# Revit family: Haworth_BeHold_PersonalStorageTower_HingedBookcase_24Wide
name_source: partatom
category: Furniture Systems
revit_build: Autodesk Revit 2018 (Build: 20170223_1515(x64)
units: mm (PartAtom-declared; Revit-internal decimal feet)

## family parameters
Always vertical = Yes
Cut with Voids When Loaded = No
OmniClass Number = 23.40.70.14.64.21
OmniClass Title = Systems Furniture
Part Type = Normal
Room Calculation Point = No
Round Connector Dimension = Use Diameter
Shared = No
Work Plane-Based = No

## types (8) — shared parameters
Actual Width = 24"
Assembly Code = E2020200
Blade Pull = No
Blade Pull Length = 15 29/64"
Bookcase Width = 15 41/64"
Bottom Case Offset = 1/2"
Bottom Drawer Offset = 1 3/8"
Case Thickness = 3/4"
Classic Pull = No
Classic Pull Length = 7 1/2"
Cresent Pull = No
Custom Size = No
Description = Haworth - Be_Hold - Personal Storage Tower - Hinged Door
Drawer Width = 15 33/64"
Glide Finish = Haworth _ Polymer _ Slate
Linear Pull = No
Linear Pull Length = 7 1/2"
Manufacturer = Haworth
Max. Depth = 24"
Max. Height = 65"
Max. Width = 15"
Min. Depth = 18"
Min. Height = 41"
Min. Width = 15"
Model = Haworth Be_Hold
Revision Number = 1
Shelf 1 Offset = 26 3/4"
Size = Verify Final Dim. w/ Haworth
Standard Depths = 18, 24 in.
Standard Heights = 41, 49, 57, 65 in.
Storage Height = 28"
Sustainability Info = https://www.haworth.com
Top Thickness = 3/4"
Total Drawer Height = 26 1/2"
URL = www.haworth.com
URL - Product = https://www.haworth.com
Valet Door Width = 8 15/64"
Warranty = http://www.haworth.com
Wing Drawer Pull Length = 8 5/16"
Wing Pull = Yes
With Lock = Yes

## per-type parameters (varying)
- B/B/F - 24d 65h - Inset Back: 3 Drawer Control=Yes; Actual Depth=24"; Actual Height=65"; Back Case Back Control=3/16"; Back Case Side Control=3/4"; Bookcase Door Height=36 1/8"; Bookcase Door Pull Offset=18 1/16"; Bottom Drawer Height=13 1/8"; Box Box File=Yes; Depth=24"; Distance Between Drawer=1/4"; File File=No; Height=65"; Inset Style=Yes; Middle Drawer Height=6 9/16"; Proud Style=No; Shelf 2 Control=Yes; Shelf 2 Offset=49"; Side Case Back Control=0"; Top Case Back Control=3/16"; Top Drawer Height=6 9/16"; Valet Door Height=62 3/4"; Valet Door Pull Offset=44 11/16"; Valet Door Wing Pull Length=16 3/4"; Wing Door Pull Length=16 3/4"
- B/B/F - 24d 57h - Inset Back: 3 Drawer Control=Yes; Actual Depth=24"; Actual Height=57"; Back Case Back Control=3/16"; Back Case Side Control=3/4"; Bookcase Door Height=28 1/8"; Bookcase Door Pull Offset=14 1/16"; Bottom Drawer Height=13 1/8"; Box Box File=Yes; Depth=24"; Distance Between Drawer=1/4"; File File=No; Height=57"; Inset Style=Yes; Middle Drawer Height=6 9/16"; Proud Style=No; Shelf 2 Control=Yes; Shelf 2 Offset=41"; Side Case Back Control=0"; Top Case Back Control=3/16"; Top Drawer Height=6 9/16"; Valet Door Height=54 3/4"; Valet Door Pull Offset=40 11/16"; Valet Door Wing Pull Length=13 1/8"; Wing Door Pull Length=13 1/8"
- B/B/F - 18d 49h - Inset Back: 3 Drawer Control=Yes; Actual Depth=18"; Actual Height=49"; Back Case Back Control=3/16"; Back Case Side Control=3/4"; Bookcase Door Height=20 1/8"; Bookcase Door Pull Offset=10 1/16"; Bottom Drawer Height=13 1/8"; Box Box File=Yes; Depth=18"; Distance Between Drawer=1/4"; File File=No; Height=49"; Inset Style=Yes; Middle Drawer Height=6 9/16"; Proud Style=No; Shelf 2 Control=Yes; Shelf 2 Offset=32 5/16"; Side Case Back Control=0"; Top Case Back Control=3/16"; Top Drawer Height=6 9/16"; Valet Door Height=46 3/4"; Valet Door Pull Offset=36 11/16"; Valet Door Wing Pull Length=8 5/16"; Wing Door Pull Length=8 5/16"
- B/B/F - 18d 41h - Inset Back: 3 Drawer Control=Yes; Actual Depth=18"; Actual Height=49"; Back Case Back Control=3/16"; Back Case Side Control=3/4"; Bookcase Door Height=20 1/8"; Bookcase Door Pull Offset=10 1/16"; Bottom Drawer Height=13 1/8"; Box Box File=Yes; Depth=18"; Distance Between Drawer=1/4"; File File=No; Height=49"; Inset Style=Yes; Middle Drawer Height=6 9/16"; Proud Style=No; Shelf 2 Control=Yes; Shelf 2 Offset=32 5/16"; Side Case Back Control=0"; Top Case Back Control=3/16"; Top Drawer Height=6 9/16"; Valet Door Height=46 3/4"; Valet Door Pull Offset=36 11/16"; Valet Door Wing Pull Length=8 5/16"; Wing Door Pull Length=8 5/16"
- F/F - 18d 49h - Proud Back: 3 Drawer Control=No; Actual Depth=18"; Actual Height=49"; Back Case Back Control=0"; Back Case Side Control=0"; Bookcase Door Height=20 1/8"; Bookcase Door Pull Offset=10 1/16"; Bottom Drawer Height=13 3/16"; Box Box File=No; Depth=18"; Distance Between Drawer=1/8"; File File=Yes; Height=49"; Inset Style=No; Middle Drawer Height=6 19/32"; Proud Style=Yes; Shelf 2 Control=Yes; Shelf 2 Offset=32 5/16"; Side Case Back Control=3/4"; Top Case Back Control=0"; Top Drawer Height=13 3/16"; Valet Door Height=46 3/4"; Valet Door Pull Offset=36 11/16"; Valet Door Wing Pull Length=8 5/16"; Wing Door Pull Length=8 5/16"
- F/F - 18d 41h - Proud Back: 3 Drawer Control=No; Actual Depth=18"; Actual Height=41"; Back Case Back Control=0"; Back Case Side Control=0"; Bookcase Door Height=12 1/8"; Bookcase Door Pull Offset=5 117/256"; Bottom Drawer Height=13 3/16"; Box Box File=No; Depth=18"; Distance Between Drawer=1/8"; File File=Yes; Height=41"; Inset Style=No; Middle Drawer Height=6 19/32"; Proud Style=Yes; Shelf 2 Control=No; Shelf 2 Offset=32 5/16"; Side Case Back Control=3/4"; Top Case Back Control=0"; Top Drawer Height=13 3/16"; Valet Door Height=38 3/4"; Valet Door Pull Offset=32 21/256"; Valet Door Wing Pull Length=6 1/2"; Wing Door Pull Length=6 1/2"
- F/F - 24d 57h - Proud Back: 3 Drawer Control=No; Actual Depth=24"; Actual Height=57"; Back Case Back Control=0"; Back Case Side Control=0"; Bookcase Door Height=28 1/8"; Bookcase Door Pull Offset=14 1/16"; Bottom Drawer Height=13 3/16"; Box Box File=No; Depth=24"; Distance Between Drawer=1/8"; File File=Yes; Height=57"; Inset Style=No; Middle Drawer Height=6 19/32"; Proud Style=Yes; Shelf 2 Control=Yes; Shelf 2 Offset=41"; Side Case Back Control=3/4"; Top Case Back Control=0"; Top Drawer Height=13 3/16"; Valet Door Height=54 3/4"; Valet Door Pull Offset=40 11/16"; Valet Door Wing Pull Length=13 1/8"; Wing Door Pull Length=13 1/8"
- F/F - 24d 65h - Proud Back: 3 Drawer Control=No; Actual Depth=24"; Actual Height=65"; Back Case Back Control=0"; Back Case Side Control=0"; Bookcase Door Height=36 1/8"; Bookcase Door Pull Offset=18 1/16"; Bottom Drawer Height=13 3/16"; Box Box File=No; Depth=24"; Distance Between Drawer=1/8"; File File=Yes; Height=65"; Inset Style=No; Middle Drawer Height=6 19/32"; Proud Style=Yes; Shelf 2 Control=Yes; Shelf 2 Offset=49"; Side Case Back Control=3/4"; Top Case Back Control=0"; Top Drawer Height=13 3/16"; Valet Door Height=62 3/4"; Valet Door Pull Offset=44 11/16"; Valet Door Wing Pull Length=16 3/4"; Wing Door Pull Length=16 3/4"

## geometry (parser evidence)
native form markers: Sweep x9
no freeform markers — native parametric forms only
